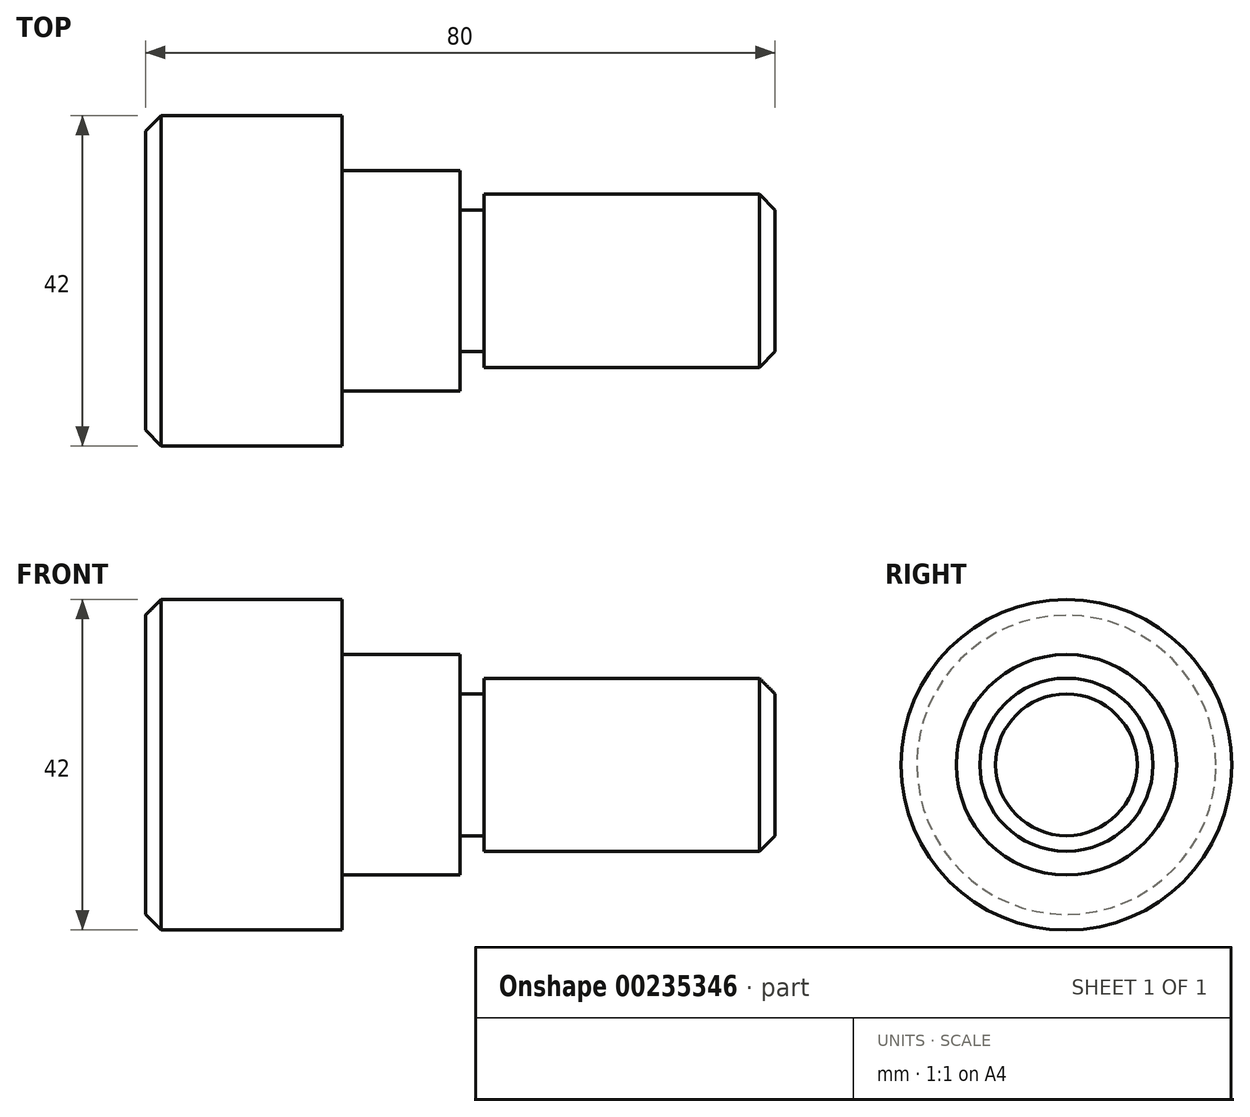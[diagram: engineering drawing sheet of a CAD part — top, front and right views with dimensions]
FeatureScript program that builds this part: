
annotation { "Feature Type Name" : "Feature", "Feature Type Description" : "" }
export const myFeature = defineFeature(function(context is Context, id is Id, definition is map)
    precondition{}
    {
        {
            var Q0;
            Q0=qCreatedBy(makeId("Front.planeOp"),FACE);
            var sketch = newSketch(context, id + "F0", { "sketchPlane" : qUnion([Q0])});
            skLineSegment(sketch, "E0", {"start": v(0, 0) * mm, "end": v(129.31, 0) * mm, "construction": true});
            skLineSegment(sketch, "E1", {"start": v(10, 0) * mm, "end": v(10, 19) * mm});
            skLineSegment(sketch, "E2", {"start": v(10, 19) * mm, "end": v(12, 21) * mm});
            skLineSegment(sketch, "E3", {"start": v(12, 21) * mm, "end": v(35, 21) * mm});
            skLineSegment(sketch, "E4", {"start": v(35, 21) * mm, "end": v(35, 0) * mm});
            skLineSegment(sketch, "E5", {"start": v(35, 0) * mm, "end": v(12, 0) * mm});
            skLineSegment(sketch, "E6", {"start": v(12, 21) * mm, "end": v(12, 0) * mm});
            skLineSegment(sketch, "E7", {"start": v(35, 14) * mm, "end": v(50, 14) * mm});
            skLineSegment(sketch, "E8", {"start": v(50, 14) * mm, "end": v(50, 0) * mm});
            skLineSegment(sketch, "E9", {"start": v(50, 0) * mm, "end": v(35, 0) * mm});
            skLineSegment(sketch, "E10", {"start": v(50, 9) * mm, "end": v(53, 9) * mm});
            skLineSegment(sketch, "E11", {"start": v(53, 9) * mm, "end": v(53, 0) * mm});
            skLineSegment(sketch, "E12", {"start": v(53, 0) * mm, "end": v(50, 0) * mm});
            skLineSegment(sketch, "E13", {"start": v(53, 9) * mm, "end": v(53, 11) * mm});
            skLineSegment(sketch, "E14", {"start": v(53, 11) * mm, "end": v(88, 11) * mm});
            skLineSegment(sketch, "E15", {"start": v(88, 11) * mm, "end": v(88, 0) * mm});
            skLineSegment(sketch, "E16", {"start": v(88, 0) * mm, "end": v(53, 0) * mm});
            skLineSegment(sketch, "E17", {"start": v(88, 11) * mm, "end": v(90, 9) * mm});
            skLineSegment(sketch, "E18", {"start": v(90, 9) * mm, "end": v(90, 0) * mm});
            skLineSegment(sketch, "E19", {"start": v(90, 0) * mm, "end": v(88, 0) * mm});
            skLineSegment(sketch, "E20", {"start": v(10, 0) * mm, "end": v(12, 0) * mm});
            skSolve(sketch);
        }
        {
            var Q0;
            Q0=makeQuery(id+"F0.imprint","IMPRINT",FACE,{"disambiguationData":[TD([[makeQuery(id+"F0.imprint","IMPRINT",EDGE,{"derivedFrom":sQuery(id+"F0.wireOp",EDGE,"E1")}),-1.0]])]});
            var Q1;
            {var subQ3=sQuery(id+"F0.wireOp",EDGE,"E3");Q1=makeQuery(id+"F0.imprint","IMPRINT",FACE,{"disambiguationData":[TD([[makeQuery(id+"F0.imprint","IMPRINT",EDGE,{"derivedFrom":subQ3}),-1.0]])]});}
            var Q2;
            {var subQ3=sQuery(id+"F0.wireOp",EDGE,"E7");Q2=makeQuery(id+"F0.imprint","IMPRINT",FACE,{"disambiguationData":[TD([[makeQuery(id+"F0.imprint","IMPRINT",EDGE,{"derivedFrom":subQ3}),-1.0]])]});}
            var Q3;
            {var subQ2=sQuery(id+"F0.wireOp",EDGE,"E10");Q3=makeQuery(id+"F0.imprint","IMPRINT",FACE,{"disambiguationData":[TD([[makeQuery(id+"F0.imprint","IMPRINT",EDGE,{"derivedFrom":subQ2}),-1.0]])]});}
            var Q4;
            Q4=makeQuery(id+"F0.imprint","IMPRINT",FACE,{"disambiguationData":[TD([[makeQuery(id+"F0.imprint","IMPRINT",EDGE,{"derivedFrom":sQuery(id+"F0.wireOp",EDGE,"E11")}),1.0]])]});
            var Q5;
            Q5=makeQuery(id+"F0.imprint","IMPRINT",FACE,{"disambiguationData":[TD([[makeQuery(id+"F0.imprint","IMPRINT",EDGE,{"derivedFrom":sQuery(id+"F0.wireOp",EDGE,"E15")}),1.0]])]});
            var Q6;
            Q6=sQuery(id+"F0.wireOp",EDGE,"E0");
            revolve(context, id + "F1", {"entities" : qUnion([Q0, Q1, Q2, Q3, Q4, Q5]), "axis" : qUnion([Q6]), "revolveType" : RevolveType.FULL});
        }
    });
